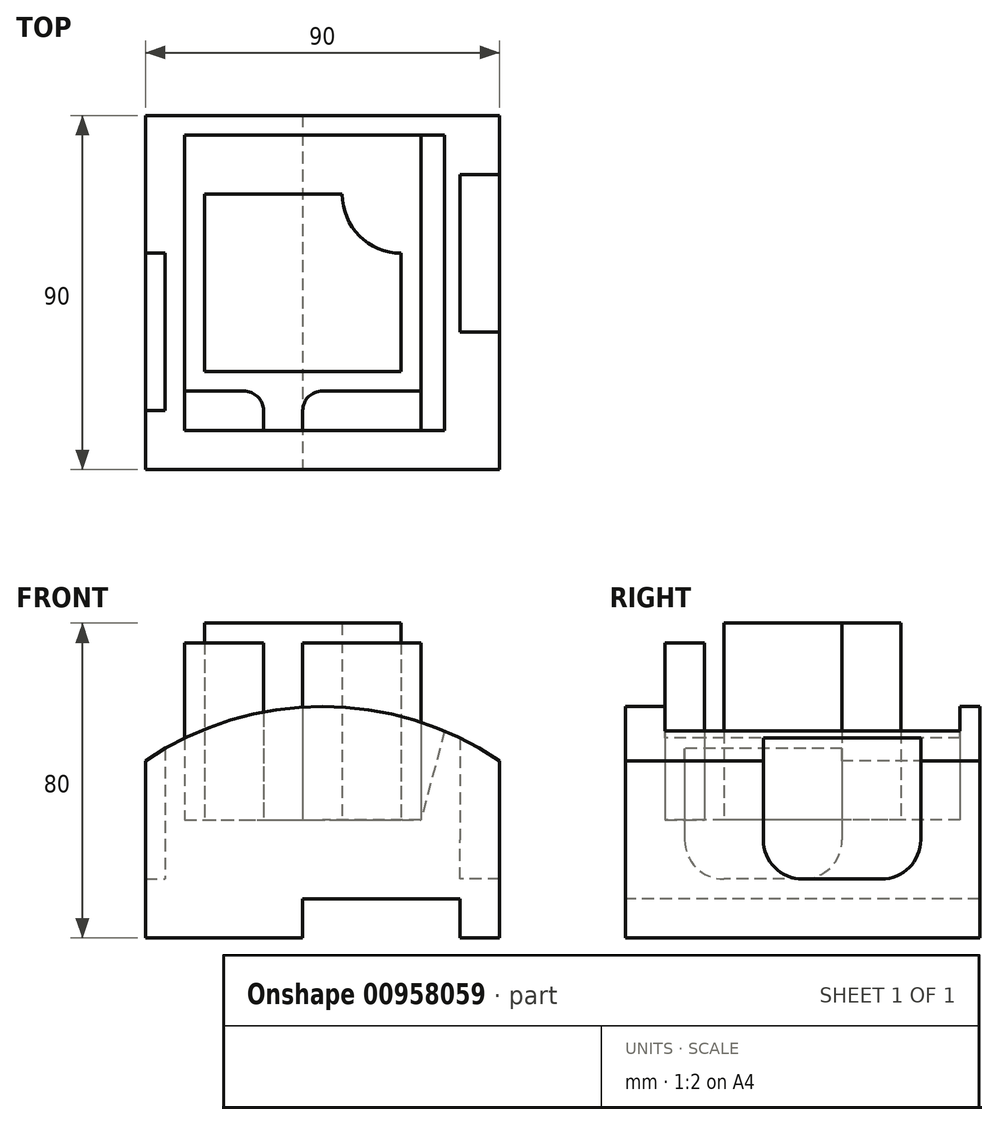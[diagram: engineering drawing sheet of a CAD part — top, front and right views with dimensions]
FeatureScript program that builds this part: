
annotation { "Feature Type Name" : "Feature", "Feature Type Description" : "" }
export const myFeature = defineFeature(function(context is Context, id is Id, definition is map)
    precondition{}
    {
        {
            var Q0;
            Q0=qCreatedBy(makeId("Front.planeOp"),FACE);
            var sketch = newSketch(context, id + "F0", { "sketchPlane" : qUnion([Q0])});
            skLineSegment(sketch, "E0.bottom", {"start": v(0, 0) * mm, "end": v(40, 0) * mm});
            skLineSegment(sketch, "E0.left", {"start": v(0, 0) * mm, "end": v(0, 45) * mm});
            skLineSegment(sketch, "E0.right", {"start": v(90, 0) * mm, "end": v(90, 45) * mm});
            skLineSegment(sketch, "E1.top", {"start": v(40, 10) * mm, "end": v(80, 10) * mm});
            skLineSegment(sketch, "E1.left", {"start": v(40, 0) * mm, "end": v(40, 10) * mm});
            skLineSegment(sketch, "E1.right", {"start": v(80, 0) * mm, "end": v(80, 10) * mm});
            skArc(sketch, "E2", {"start": v(90, 45) * mm, "mid": v(45, 58.86) * mm, "end": v(0, 45) * mm});
            skLineSegment(sketch, "E3.trimOffspring", {"start": v(80, 0) * mm, "end": v(80, 0) * mm});
            skLineSegment(sketch, "E4", {"start": v(80, 0) * mm, "end": v(90, 0) * mm});
            skSolve(sketch);
        }
        {
            var Q0;
            Q0 = qSketchRegion(id + "F0", true);
            extrude(context, id + "F1", {"entities" : qUnion([Q0]), "oppositeDirection" : true, "depth" : 90 * mm, "offsetDistance" : 25 * mm});
        }
        {
            var Q0;
            Q0=makeQuery(id+"F1.opExtrude","SWEPT_FACE",FACE,{"disambiguationData":[OSD([sQuery(id+"F0.wireOp",EDGE,"E0.bottom")])]});
            cPlane(context, id + "F2", {"entities" : qUnion([Q0]), "cplaneType" : CPlaneType.OFFSET, "offset" : 30 * mm, "oppositeDirection" : true, "width" : 150 * mm, "height" : 150 * mm});
        }
        {
            var Q0;
            Q0=qCreatedBy(id+"F2.planeOp",FACE);
            var sketch = newSketch(context, id + "F3", { "sketchPlane" : qUnion([Q0])});
            skLineSegment(sketch, "E5.bottom", {"start": v(10, -85) * mm, "end": v(70, -85) * mm});
            skLineSegment(sketch, "E5.top", {"start": v(10, -10) * mm, "end": v(70, -10) * mm});
            skLineSegment(sketch, "E5.left", {"start": v(10, -85) * mm, "end": v(10, -10) * mm});
            skLineSegment(sketch, "E5.right", {"start": v(70, -85) * mm, "end": v(70, -10) * mm});
            skSolve(sketch);
        }
        {
            var Q0;
            Q0 = qSketchRegion(id + "F3", true);
            extrude(context, id + "F4", {"entities" : qUnion([Q0]), "operationType" : NewBodyOperationType.REMOVE, "endBound" : BoundingType.THROUGH_ALL, "oppositeDirection" : true, "depth" : 25 * mm, "offsetDistance" : 25 * mm});
        }
        {
            var Q0;
            Q0=makeQuery(id+"F4.boolean.opBoolean","COPY",FACE,{"derivedFrom":makeQuery(id+"F4.opExtrude","SWEPT_FACE",FACE,{"disambiguationData":[OSD([sQuery(id+"F3.wireOp",EDGE,"E5.bottom")])]})});
            var sketch = newSketch(context, id + "F5", { "sketchPlane" : qUnion([Q0])});
            skLineSegment(sketch, "E6", {"start": v(70, 30) * mm, "end": v(70, 54.85) * mm});
            skLineSegment(sketch, "E7", {"start": v(70, 54.85) * mm, "end": v(76.66, 54.85) * mm});
            skLineSegment(sketch, "E8", {"start": v(76.66, 54.85) * mm, "end": v(70, 30) * mm});
            skSolve(sketch);
        }
        {
            var Q0;
            Q0 = qSketchRegion(id + "F5", true);
            var Q1;
            Q1=makeQuery(id+"F4.boolean.opBoolean","COPY",FACE,{"derivedFrom":makeQuery(id+"F4.opExtrude","SWEPT_FACE",FACE,{"disambiguationData":[OSD([sQuery(id+"F3.wireOp",EDGE,"E5.top")])]})});
            extrude(context, id + "F6", {"entities" : qUnion([Q0]), "operationType" : NewBodyOperationType.REMOVE, "endBound" : BoundingType.UP_TO_SURFACE, "depth" : 25 * mm, "endBoundEntityFace" : qUnion([Q1]), "offsetDistance" : 25 * mm});
        }
        {
            var Q0;
            Q0=makeQuery(id+"F4.boolean.opBoolean","COPY",FACE,{"derivedFrom":makeQuery(id+"F4.opExtrude","CAP_FACE",FACE,{"disambiguationData":[OSD([sQuery(id+"F3.wireOp",EDGE,"E5.bottom"),sQuery(id+"F3.wireOp",EDGE,"E5.top"),sQuery(id+"F3.wireOp",EDGE,"E5.left"),sQuery(id+"F3.wireOp",EDGE,"E5.right")])],"isStart":true})});
            var sketch = newSketch(context, id + "F7", { "sketchPlane" : qUnion([Q0])});
            skLineSegment(sketch, "E9.bottom", {"start": v(10, 10) * mm, "end": v(30, 10) * mm});
            skLineSegment(sketch, "E9.top", {"start": v(10, 20) * mm, "end": v(30, 20) * mm});
            skLineSegment(sketch, "E9.left", {"start": v(10, 10) * mm, "end": v(10, 20) * mm});
            skLineSegment(sketch, "E9.right", {"start": v(30, 10) * mm, "end": v(30, 20) * mm});
            skLineSegment(sketch, "E10.bottom", {"start": v(70, 10) * mm, "end": v(40, 10) * mm});
            skLineSegment(sketch, "E10.top", {"start": v(70, 20) * mm, "end": v(40, 20) * mm});
            skLineSegment(sketch, "E10.left", {"start": v(70, 10) * mm, "end": v(70, 20) * mm});
            skLineSegment(sketch, "E10.right", {"start": v(40, 10) * mm, "end": v(40, 20) * mm});
            skSolve(sketch);
        }
        {
            var Q0;
            Q0 = qSketchRegion(id + "F7", true);
            extrude(context, id + "F8", {"entities" : qUnion([Q0]), "operationType" : NewBodyOperationType.ADD, "depth" : 45 * mm, "offsetDistance" : 25 * mm});
        }
        {
            var Q0;
            Q0=makeQuery(id+"F8.opExtrude","SWEPT_EDGE",EDGE,{"disambiguationData":[OSD([sQuery(id+"F7.wireOp",EDGE,"E10.top"),sQuery(id+"F7.wireOp",EDGE,"E10.right")])]});
            var Q1;
            Q1=makeQuery(id+"F8.opExtrude","SWEPT_EDGE",EDGE,{"disambiguationData":[OSD([sQuery(id+"F7.wireOp",EDGE,"E9.top"),sQuery(id+"F7.wireOp",EDGE,"E9.right")])]});
            fillet(context, id + "F9", {"entities" : qUnion([Q0, Q1]), "radius" : 5 * mm, "tangentPropagation" : true, "allowEdgeOverflow" : false});
        }
        {
            var Q0;
            Q0=makeQuery(id+"F4.boolean.opBoolean","COPY",FACE,{"derivedFrom":makeQuery(id+"F4.opExtrude","CAP_FACE",FACE,{"disambiguationData":[OSD([sQuery(id+"F3.wireOp",EDGE,"E5.bottom"),sQuery(id+"F3.wireOp",EDGE,"E5.top"),sQuery(id+"F3.wireOp",EDGE,"E5.left"),sQuery(id+"F3.wireOp",EDGE,"E5.right")])],"isStart":true})});
            var sketch = newSketch(context, id + "F10", { "sketchPlane" : qUnion([Q0])});
            skLineSegment(sketch, "E11.bottom", {"start": v(15, 70) * mm, "end": v(50, 70) * mm});
            skLineSegment(sketch, "E11.top", {"start": v(15, 25) * mm, "end": v(65, 25) * mm});
            skLineSegment(sketch, "E11.left", {"start": v(15, 70) * mm, "end": v(15, 25) * mm});
            skLineSegment(sketch, "E11.right", {"start": v(65, 55) * mm, "end": v(65, 25) * mm});
            skArc(sketch, "E12", {"start": v(50, 70) * mm, "mid": v(54.4, 59.4) * mm, "end": v(65, 55) * mm});
            skSolve(sketch);
        }
        {
            var Q0;
            Q0 = qSketchRegion(id + "F10", true);
            extrude(context, id + "F11", {"entities" : qUnion([Q0]), "operationType" : NewBodyOperationType.ADD, "depth" : 50 * mm, "offsetDistance" : 25 * mm});
        }
        {
            var Q0;
            Q0=makeQuery(id+"F1.opExtrude","SWEPT_FACE",FACE,{"disambiguationData":[OSD([sQuery(id+"F0.wireOp",EDGE,"E0.bottom")])]});
            cPlane(context, id + "F12", {"entities" : qUnion([Q0]), "cplaneType" : CPlaneType.OFFSET, "offset" : 15 * mm, "oppositeDirection" : true, "width" : 150 * mm, "height" : 150 * mm});
        }
        {
            var Q0;
            Q0=qCreatedBy(id+"F12.planeOp",FACE);
            var sketch = newSketch(context, id + "F13", { "sketchPlane" : qUnion([Q0])});
            skLineSegment(sketch, "E13.bottom", {"start": v(0, -55) * mm, "end": v(5, -55) * mm});
            skLineSegment(sketch, "E13.top", {"start": v(0, -15) * mm, "end": v(5, -15) * mm});
            skLineSegment(sketch, "E13.left", {"start": v(0, -55) * mm, "end": v(0, -15) * mm});
            skLineSegment(sketch, "E13.right", {"start": v(5, -55) * mm, "end": v(5, -15) * mm});
            skLineSegment(sketch, "E14.bottom", {"start": v(90, -75) * mm, "end": v(80, -75) * mm});
            skLineSegment(sketch, "E14.top", {"start": v(90, -35) * mm, "end": v(80, -35) * mm});
            skLineSegment(sketch, "E14.left", {"start": v(90, -75) * mm, "end": v(90, -35) * mm});
            skLineSegment(sketch, "E14.right", {"start": v(80, -75) * mm, "end": v(80, -35) * mm});
            skSolve(sketch);
        }
        {
            var Q0;
            Q0 = qSketchRegion(id + "F13", true);
            extrude(context, id + "F14", {"entities" : qUnion([Q0]), "operationType" : NewBodyOperationType.REMOVE, "endBound" : BoundingType.THROUGH_ALL, "oppositeDirection" : true, "depth" : 25 * mm, "offsetDistance" : 25 * mm});
        }
        {
            var Q0;
            Q0=makeQuery(id+"F14.boolean.opBoolean","COPY",EDGE,{"derivedFrom":makeQuery(id+"F14.opExtrude","CAP_EDGE",EDGE,{"disambiguationData":[OSD([sQuery(id+"F13.wireOp",EDGE,"E13.bottom")])],"isStart":true})});
            var Q1;
            Q1=makeQuery(id+"F14.boolean.opBoolean","COPY",EDGE,{"derivedFrom":makeQuery(id+"F14.opExtrude","CAP_EDGE",EDGE,{"disambiguationData":[OSD([sQuery(id+"F13.wireOp",EDGE,"E13.top")])],"isStart":true})});
            var Q2;
            Q2=makeQuery(id+"F14.boolean.opBoolean","COPY",EDGE,{"derivedFrom":makeQuery(id+"F14.opExtrude","CAP_EDGE",EDGE,{"disambiguationData":[OSD([sQuery(id+"F13.wireOp",EDGE,"E14.top")])],"isStart":true})});
            var Q3;
            Q3=makeQuery(id+"F14.boolean.opBoolean","COPY",EDGE,{"derivedFrom":makeQuery(id+"F14.opExtrude","CAP_EDGE",EDGE,{"disambiguationData":[OSD([sQuery(id+"F13.wireOp",EDGE,"E14.bottom")])],"isStart":true})});
            fillet(context, id + "F15", {"entities" : qUnion([Q0, Q1, Q2, Q3]), "radius" : 10 * mm, "tangentPropagation" : true, "allowEdgeOverflow" : false});
        }
    });
